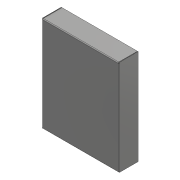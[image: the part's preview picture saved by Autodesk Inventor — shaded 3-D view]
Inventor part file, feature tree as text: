
AUTODESK INVENTOR PART (.ipt)
format: ipt  version: 2018 (Build 220112000, 112)  size: 128,000 bytes
history: native  units: mm
features: sheet_metal_op x9, sketch x3, other x3
ambient origin geometry x8: Origin, YZ Plane, XZ Plane, XY Plane, X Axis, Y Axis, Z Axis, Center Point
bodies: Solid1 (feature_tree)
feature tree (15):
  sheet_metal_op  "Contour Flange1"
  sheet_metal_op  "Flange1"
  sheet_metal_op  "Flange2"
  sketch  "Sketch2"  dims[d2=200.0mm]
  other  "Plate1"
  sheet_metal_op  "Bend1"
  sheet_metal_op  "Corner1"
  sketch  "Sketch3"  dims[d3=50.0mm]
  other  "Plate2"
  sheet_metal_op  "Bend2"
  sheet_metal_op  "Corner2"
  sketch  "Sketch4"  dims[d4=1.0mm d5=1.0mm d6=0.5mm d7=2.0mm d8=1.0mm d9=250.0mm d10=1.0mm d11=1.0mm d12=4.0mm d13=1.0mm d14=1.0mm d15=1.0mm d16=0.5mm d17=2.0mm d18=1.0mm d19=25.0mm d20=90.0deg d21=1.0mm d22=0.0mm d23=4.0mm d24=1.0mm d25=1.0mm d26=1.0mm d27=0.5mm d28=2.0mm d29=1.0mm d30=25.0mm d31=90.0deg d32=1.0mm d33=0.0mm d34=4.0mm d35=1.0mm d36=1.0mm]
  other  "Plate3"
  sheet_metal_op  "Bend3"
  sheet_metal_op  "Corner3"
